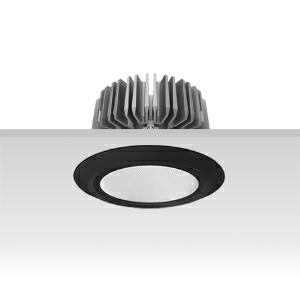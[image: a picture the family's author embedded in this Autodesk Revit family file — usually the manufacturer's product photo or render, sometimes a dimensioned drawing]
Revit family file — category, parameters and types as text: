
# Revit family: 3f_filippi_-_3f_reno_bianco_ampio_3f_filippi_-_30349_a01047_-_3f_reno_150_wh_3000-840_wide___smp_bk_ce06
name_source: partatom
category: Lighting Fixtures
units: mm (PartAtom-declared; Revit-internal decimal feet)

## family parameters
Cut with Voids When Loaded = No
Host = Face
Light Source = No
Part Type = Normal
Room Calculation Point = No
Round Connector Dimension = Use Diameter
Shared = No

## types (1)
- 3F Filippi - 3F Reno Bianco Ampio (1 x LED, 2316 lm, 28 W, 4000 K)
    Apparent Load = 28 VA
    Approval mark = CE
    CIE Flux Codes = 73 92 98 100 100
    Color Rendering = 80
    Color Temperature = 4000 K
    Control Gear = Electronic ballast
    Default Elevation = 1800 mm
    Description = ILLUMINOTECHNICAL
Luminous efficiency 100% (DLOR 100%, ULOR 0%).
Initial luminous flux of the luminaire 2316 lm.
Direct symmetric wide distribution.
Installation Interdistance Transv.D = 1.01 x hu - Long.D = 1.00 x hu.
Tabular UGR (CIE 117 - 4H-8H; S=0.25H; 70/50/20): RUG 24.4 - 24.5.
Beam angle: 70° - 70°.
Luminous efficacy 83 lm/W.
Lifetime (L90/B10): 30000 h. (tq+25°C)
Lifetime (L85/B10): 50000 h. (tq+25°C)
Lifetime (L70/B10): 80000 h. (tq+25°C)
Sudden decreased luminous flux after 50000 hours: 0% (C0).
Photobiological safety in compliance with IEC/TR 62778: RG0 risk exempt, (IEC 62471).
In compliance with IEC/EN 62722-2-1 - IEC/EN 62717 standards.

SOURCE
Compact LED module 3000/840.
Energy efficiency class (UE 2019/2020 - UE 2019/2015): D.
CIE 13.3 Colour rendering index: CRI >80 (R9 <50%).
IES TM-30 Fidelity Index: Rf = 84 Rg = 95.
CCT nominal colour temperature 4000 K.
Colour initial tolerance (MacAdam): SDCM 3.
Zhaga Book 3 compliant.

MECHANICAL
Passive heat dissipator in die-casting aluminium, oversized, for optimum thermal management of the LED module.
Parabolic element with graduated/concentric rings in white polycarbonate.
Transparent external lens with glossy and satin differentiated surfaces, with a cooling and anti-insect system in methacrylate (PMMA).
Fastening spring clips in stainless steel.
Dimensions: diameter 176 mm, height 111 mm. Weight 1.39 kg.
IP44 protection degree for exposed part, IP20 for recessed part.
Mechanical strength to impacts IK05 (0.7 joule).
Glow-wire test resistance 650°C.

ELECTRICAL
Wiring on a separate unit.
Halogen Free electronic wiring 230V-50/60Hz, power factor 0.95, THD <25%, constant output current, SELV, class II, 1 driver.
Power of the luminaire 28 W.
ENEC - CE.
SAFE FLICKER: PstLM=<1 and SVM=<0.4 (IEC TR 61547-1 and IEC TR 63158), to ensure a more comfortable and safe light.
Luminaire compliant with EN 60598-2-22 for power supply from a centralised emergency system CPSS (Central Power Supply System), not incorporated in the luminaire - high risk areas excluded. The default power and flux are 100% in AC and 100% in DC.
Ambient temperature from 0°C to +25°C.
Temperature class T6 max 85°C.
Relative humidity UR: <85%.

INSTALLATION
Pull-up recessed fitting.
False ceiling carving: 150 mm.
All accessories dedicated to this product are available on the Catalog and on our website www.3F-Filippi.com.

ACCESSORIES
A01047 - Anti-glare microprismatic SMP diffuser in methacrylate (PMMA), locked and in line with the trim, in black polycarbonate.

APPLICATIONS
Suitable product for food production plants (HACCP), IFS (Food Version 6), BRC (GSFS Food Version 7).
Environments: architectural, commercial, exhibition areas, transit areas, corridors, shops, display windows, service areas.
In false ceilings with narrow voids.

WARNING
Luminaire designed for disposal/recycling at end-of-life.
Replaceable (LED only) light source by a professional. Replaceable control gear by a professional.
    Height = 0 mm  [stored 0 ft]
    Lamp = 1 x LED
    Lamp Light Flux = 2316 lm
    Lamp Power = 28 W
    Lamp count = 1
    Length = 176 mm
    Lifetime = 50000 h
    Luminous efficacy = 83 lm/W
    Manufacturer = 3F Filippi
    ModVariant = No
    Model = 3F Filippi - 30349+A01047 - 3F Reno 150 WH 3000-840 WIDE + SMP BK
    Mounting Place = Ceiling
    Mounting Type = Recessed
    Number of Poles = 1
    OnlyDefault = Yes
    Power Factor = 1
    Product Name = 3F Filippi - 3F Reno Bianco Ampio
    Product group = recessed luminaire
    ProductGroupID = 4
    Protection Class = Protection class II
    Protection Degree = IP 20
    RLX_Detail_Level = 1
    RLX_Emergency_Light_Flux = 0 lm
    RLX_Emergency_Type = 0
    RLX_Emergency_Type_DB = No
    RlxData = <blob elided: 86277 chars, md5=f4784862>
    Socket = socket
    Standby Power = 0 W
    System Light Flux = 2316 lm
    System Power = 28 W
    Type Comments = Product without accessories
    Type Image = 3ffilippi_3f_reno_150_bk_vs_smp.jpg
    URL = http://relux.com
    VarID = ---
    Voltage = 0 V
    Weight = 0.00 kg
    Width = 0 mm  [stored 0 ft]

note: [stored X ft] marks values corroborated as IEEE doubles in the binary element streams (Revit-internal decimal feet)

## geometry (parser evidence)
native form markers: Blend x4, Sweep x11
no freeform markers — native parametric forms only
